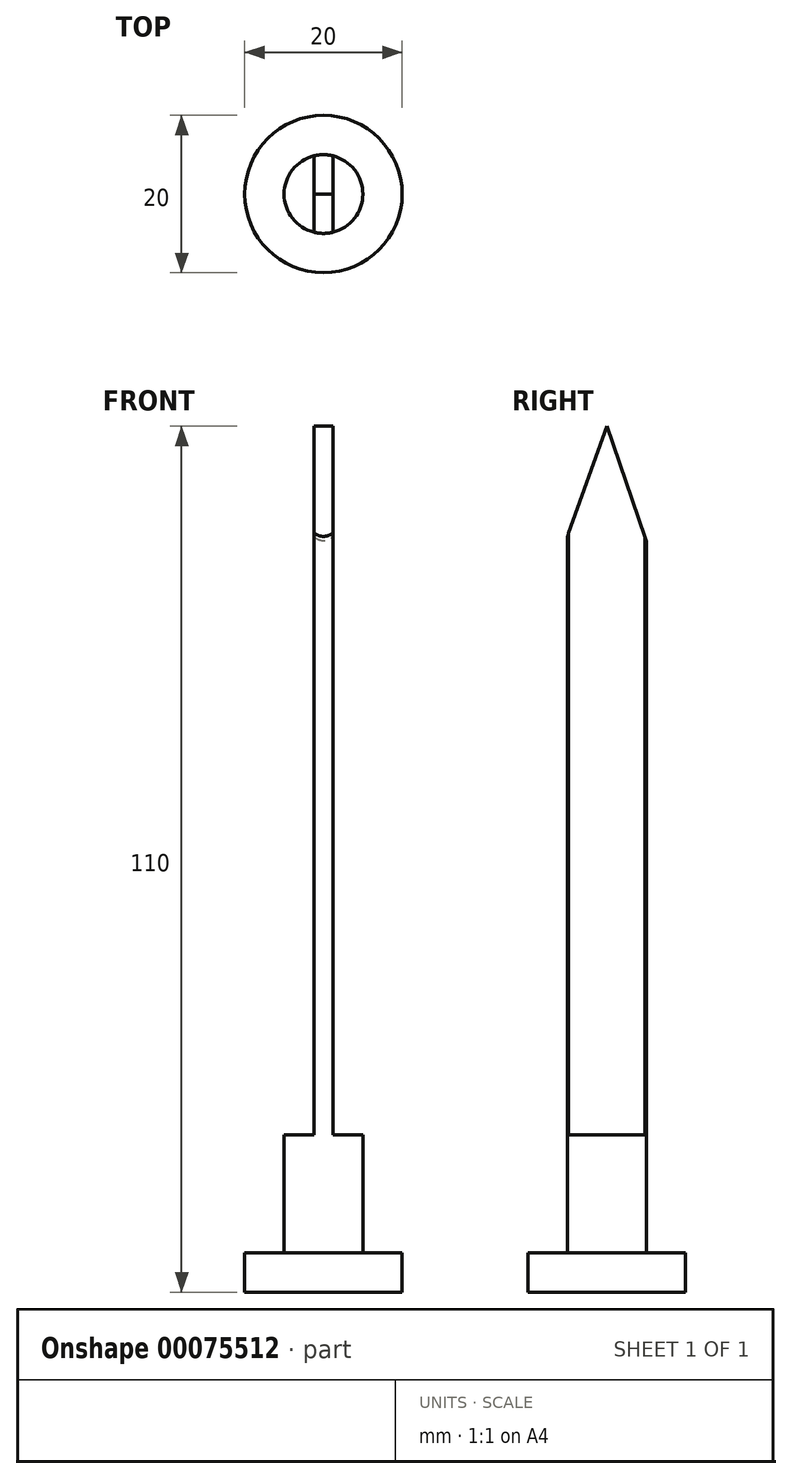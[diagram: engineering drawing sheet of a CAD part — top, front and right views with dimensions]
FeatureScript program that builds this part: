
annotation { "Feature Type Name" : "Feature", "Feature Type Description" : "" }
export const myFeature = defineFeature(function(context is Context, id is Id, definition is map)
    precondition{}
    {
        {
            var Q0;
            Q0=qCreatedBy(makeId("Top.planeOp"),FACE);
            var sketch = newSketch(context, id + "F0", { "sketchPlane" : qUnion([Q0])});
            skCircle(sketch, "E0", {"center": v(0, 0) * mm, "radius": 5 * mm});
            skCircle(sketch, "E1", {"center": v(0, 0) * mm, "radius": 10 * mm});
            skSolve(sketch);
        }
        {
            var Q0;
            Q0=makeQuery(id+"F0.imprint","IMPRINT",FACE,{"disambiguationData":[TD([[makeQuery(id+"F0.imprint","IMPRINT",EDGE,{"derivedFrom":sQuery(id+"F0.wireOp",EDGE,"E0")}),1.0]])]});
            extrude(context, id + "F1", {"entities" : qUnion([Q0]), "depth" : 125 * mm});
        }
        {
            var Q0;
            Q0=qCreatedBy(makeId("Front.planeOp"),FACE);
            var sketch = newSketch(context, id + "F2", { "sketchPlane" : qUnion([Q0])});
            skLineSegment(sketch, "E2.bottom", {"start": v(-8.22, 130) * mm, "end": v(-1.2, 130) * mm});
            skLineSegment(sketch, "E2.top", {"start": v(-8.22, 20) * mm, "end": v(-1.2, 20) * mm});
            skLineSegment(sketch, "E2.left", {"start": v(-8.22, 130) * mm, "end": v(-8.22, 20) * mm});
            skLineSegment(sketch, "E2.right", {"start": v(-1.2, 130) * mm, "end": v(-1.2, 20) * mm});
            skLineSegment(sketch, "E3.MirrorCS", {"start": v(8.22, 130) * mm, "end": v(1.2, 130) * mm});
            skLineSegment(sketch, "E4.MirrorCS", {"start": v(1.2, 130) * mm, "end": v(1.2, 20) * mm});
            skLineSegment(sketch, "E5.MirrorCS", {"start": v(8.22, 130) * mm, "end": v(8.22, 20) * mm});
            skLineSegment(sketch, "E6.MirrorCS", {"start": v(8.22, 20) * mm, "end": v(1.2, 20) * mm});
            skSolve(sketch);
        }
        {
            var Q0;
            Q0=makeQuery(id+"F2.imprint","IMPRINT",FACE,{"disambiguationData":[TD([[makeQuery(id+"F2.imprint","IMPRINT",EDGE,{"derivedFrom":sQuery(id+"F2.wireOp",EDGE,"E2.bottom")}),-1.0]])]});
            var Q1;
            Q1=makeQuery(id+"F2.imprint","IMPRINT",FACE,{"disambiguationData":[TD([[makeQuery(id+"F2.imprint","IMPRINT",EDGE,{"derivedFrom":sQuery(id+"F2.wireOp",EDGE,"E3.MirrorCS")}),1.0]])]});
            extrude(context, id + "F3", {"entities" : qUnion([Q0, Q1]), "endBound" : BoundingType.SYMMETRIC, "depth" : 25 * mm});
        }
        {
            var Q0;
            Q0=makeQuery(id+"F3.opExtrude","SWEPT_BODY",BODY,{"disambiguationData":[OSD([sQuery(id+"F2.wireOp",EDGE,"E2.bottom"),sQuery(id+"F2.wireOp",EDGE,"E2.top"),sQuery(id+"F2.wireOp",EDGE,"E2.left"),sQuery(id+"F2.wireOp",EDGE,"E2.right")])]});
            var Q1;
            Q1=makeQuery(id+"F3.opExtrude","SWEPT_BODY",BODY,{"disambiguationData":[OSD([sQuery(id+"F2.wireOp",EDGE,"E3.MirrorCS"),sQuery(id+"F2.wireOp",EDGE,"E4.MirrorCS"),sQuery(id+"F2.wireOp",EDGE,"E5.MirrorCS"),sQuery(id+"F2.wireOp",EDGE,"E6.MirrorCS")])]});
            var Q2;
            Q2=makeQuery(id+"F1.opExtrude","SWEPT_BODY",BODY,{"disambiguationData":[OSD([sQuery(id+"F0.wireOp",EDGE,"E0")])]});
            booleanBodies(context, id + "F4", {"operationType" : BooleanOperationType.SUBTRACTION, "tools" : qUnion([Q0, Q1]), "targets" : qUnion([Q2])});
        }
        {
            var Q0;
            Q0=qCreatedBy(makeId("Right.planeOp"),FACE);
            var sketch = newSketch(context, id + "F5", { "sketchPlane" : qUnion([Q0])});
            skLineSegment(sketch, "E7", {"start": v(-35.23, 130) * mm, "end": v(32.54, 130) * mm});
            skLineSegment(sketch, "E8", {"start": v(32.54, 130) * mm, "end": v(32.54, 80) * mm});
            skLineSegment(sketch, "E9", {"start": v(32.54, 80) * mm, "end": v(10.34, 80) * mm});
            skLineSegment(sketch, "E10", {"start": v(10.34, 80) * mm, "end": v(0, 110) * mm});
            skLineSegment(sketch, "E11", {"start": v(0, 110) * mm, "end": v(-10.72, 80) * mm});
            skLineSegment(sketch, "E12", {"start": v(-10.72, 80) * mm, "end": v(-35.6, 80) * mm});
            skLineSegment(sketch, "E13", {"start": v(-35.6, 80) * mm, "end": v(-35.23, 130) * mm});
            skSolve(sketch);
        }
        {
            var Q0;
            Q0=makeQuery(id+"F5.imprint","IMPRINT",FACE,{"disambiguationData":[TD([[makeQuery(id+"F5.imprint","IMPRINT",EDGE,{"derivedFrom":sQuery(id+"F5.wireOp",EDGE,"E7")}),-1.0]])]});
            extrude(context, id + "F6", {"entities" : qUnion([Q0]), "endBound" : BoundingType.SYMMETRIC, "depth" : 25 * mm});
        }
        {
            var Q0;
            Q0=makeQuery(id+"F6.opExtrude","SWEPT_BODY",BODY,{"disambiguationData":[OSD([sQuery(id+"F5.wireOp",EDGE,"E7"),sQuery(id+"F5.wireOp",EDGE,"E8"),sQuery(id+"F5.wireOp",EDGE,"E9"),sQuery(id+"F5.wireOp",EDGE,"E10"),sQuery(id+"F5.wireOp",EDGE,"E11"),sQuery(id+"F5.wireOp",EDGE,"E12"),sQuery(id+"F5.wireOp",EDGE,"E13")])]});
            var Q1;
            Q1=makeQuery(id+"F1.opExtrude","SWEPT_BODY",BODY,{"disambiguationData":[OSD([sQuery(id+"F0.wireOp",EDGE,"E0")])]});
            booleanBodies(context, id + "F7", {"operationType" : BooleanOperationType.SUBTRACTION, "tools" : qUnion([Q0]), "targets" : qUnion([Q1])});
        }
        {
            var Q0;
            Q0 = qSketchRegion(id + "F0", true);
            extrude(context, id + "F8", {"entities" : qUnion([Q0]), "operationType" : NewBodyOperationType.ADD, "depth" : 5 * mm});
        }
    });
